# Revit family: Вычислители_тепловой_энергии_R19
name_source: partatom
category: Обобщенные модели
units: mm (PartAtom-declared; Revit-internal decimal feet)

## family parameters
Всегда вертикально = Да
Может служить основой для арматурных стержней = Нет
На основе рабочей плоскости = Нет
Общий = Нет
При загрузке вырезать с полостями = Нет
Размер круглого соединителя = Использовать диаметр
Тип детали = Нормальный
Точка расчета площади = Нет

## types (1)
- Вычислители_тепловой_энергии_R19
    bt_ЕдиницыИзмерения = шт.
    bt_ИС_ЗаводИзготовитель = Пульсар
    bt_Масса = 0
    Атмосферное давление, кПа = 84 … 106,7 кПа
    Высота = 75 мм
    Горизонтальные = Нет
    Детальное описание = Предназначен для измерений и преобразований выходных аналоговых и цифровых сигналов с последующим вычислением и индикацией тепловой энергии/энергии охлаждения, объемного расхода, объема, массового расхода, массы, температуры, разности температур, давления теплоносителя, а также измерения текущего времени.
    Диапазон показаний тепловой энергии, ГДж (Гкал) = от 0 до 999999999,999
    Длина = 205 мм
    Количество дополнительных импульсных входов = 3
    Количество контролируемых тепловых систем = 2
    Количество подключаемых датчиков давления = 6
    Количество подключаемых датчиков расхода = 6
    Количество подключаемых датчиков температуры = 6
    Масса = не более 1 кг
    Напряжение питания = от встроенного элемента питания 3,6 В / от внешнего источника питания от 8 до 26 В
    Относительная влажность воздуха = не более 95%
    Поддерживаемые типы входного сигнала от датчиков давления = по току, от 4 до 20 мА / по напряжению, от 0,4 до 2 В
    Поддерживаемые типы термосопротивлений (по заказу) = PT100(100П) / PT500(500П) / PT1000
    Температура окружающей среды = от -10 до +50 °С
    Ширина = 114 мм
